# Revit family: EVJD
name_source: partatom
category: Lighting Fixtures
revit_build: Autodesk Revit 2014 (Build: 20130308_1515(x64)
units: mm (PartAtom-declared; Revit-internal decimal feet)

## types (1)
- EVJD
    Apparent Load = 70 VA
    Assembly Code = D5020200
    Color Filter = 16777215
    Connector Description = Lighting Connector
    Default Elevation = 1219.2 mm  [stored 4 ft]
    Description = The Evolution Junior is a lightweight and portable version of the advanced Evolution floodlight. It features the same single bolt access and has a range of floor and tripod stands for a variety of temporary applications.
    Dimming Lamp Color Temperature Shift = <None>
    Emit Shape Visible in Rendering = No
    Emit from Rectangle Length = 250 mm  [stored 0.82021 ft]
    Emit from Rectangle Width = 200 mm  [stored 0.656168 ft]
    Features = Installation in gas groups
IIA, IIB and IIC
Easy and quick access
for maintenance
Simple, rapid lamp replacement
and flamepath inspection
Exceptional photometric
efficiency
Available with secondary protective glass
for shot blasting applications
    Fixture distribution = Direct
    Glass = Hubbell - Glass
    Height = 535 mm
    Housing Material = Paint - Hubbell - Light Silver
    IP Rating = IP66/67
    Lamp = LED
    Length = 248 mm  [stored 0.813648 ft]
    Load Classification = Lighting
    Manufacturer = Chalmit
    Model = EVJD
    Mounting = Paint - Hubbell - Light Silver
    Photometric Web File = CHL_EVJD_070_MS HPS.ies
    Power Factor = 1
    Product Documentation Link = https://hubbellcdn.com
    Product Link = https://www.hubbell.com
    Reflector Finish = Hubbell - White Glass
    Tilt Angle = 0.00°
    URL = https://www.hubbell.com
    Voltage = 120 V
    Warranty = 5 years Warranty
    Wattage Comments = 70w
    Watts = 70 W
    Width = 280 mm  [stored 0.918635 ft]
    Wings = Paint - Hubbell - Light Silver

note: [stored X ft] marks values corroborated as IEEE doubles in the binary element streams (Revit-internal decimal feet)

## geometry (parser evidence)
native form markers: Sweep x4
no freeform markers — native parametric forms only
